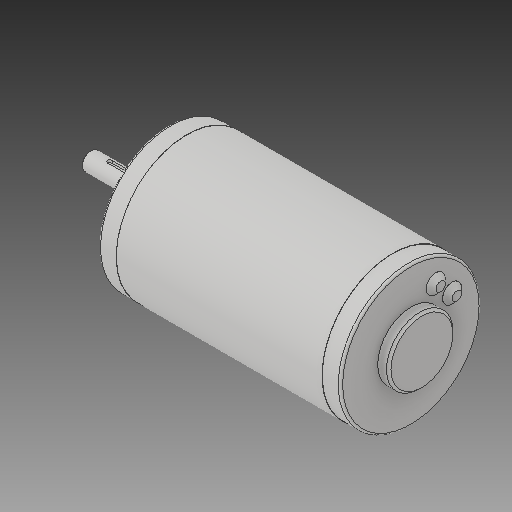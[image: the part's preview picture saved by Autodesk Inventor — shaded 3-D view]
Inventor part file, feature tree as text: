
AUTODESK INVENTOR PART (.ipt)
format: ipt  version: 2018 (Build 220112000, 112)  size: 166,912 bytes
history: native  units: in
note: dims shown in document units (in); Inventor stores cm internally (conversion verified against a paired STEP export)
features: chamfer x1
ambient origin geometry x8: Origin, YZ Plane, XZ Plane, XY Plane, X Axis, Y Axis, Z Axis, Center Point
bodies: Solid1 (feature_tree)
feature tree (1):
  chamfer  "Chamfer3"  [1 undecoded]
note: 1 required parameter value undecoded (feature->parameter linkage not recoverable at this tier; creation-order binding heuristic only, values carry confidence <= 0.55)
